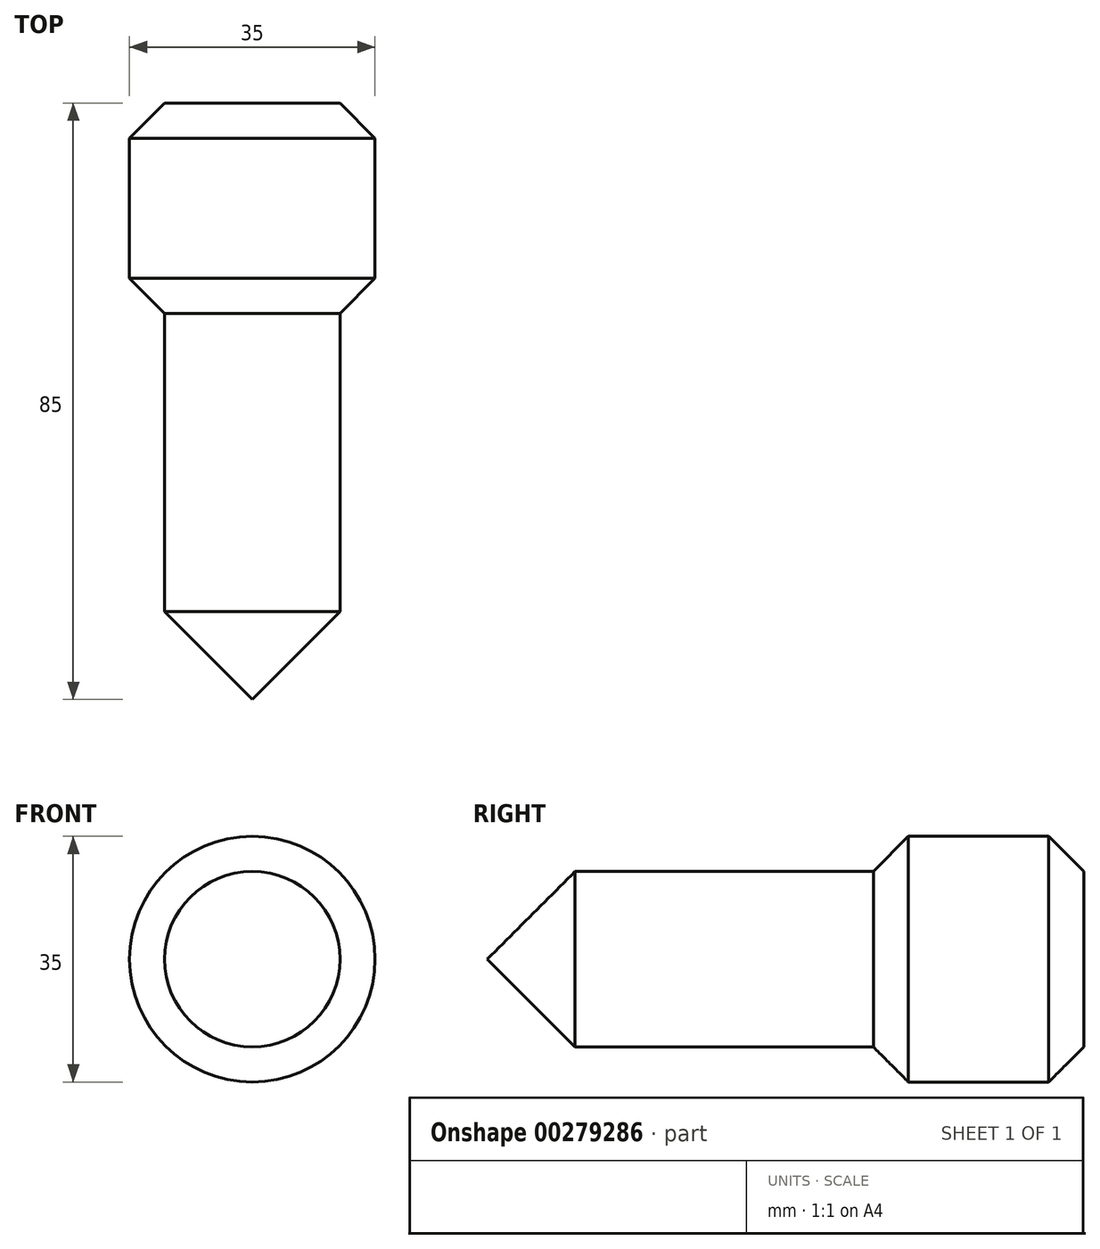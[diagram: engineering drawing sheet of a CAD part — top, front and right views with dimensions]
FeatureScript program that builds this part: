
annotation { "Feature Type Name" : "Feature", "Feature Type Description" : "" }
export const myFeature = defineFeature(function(context is Context, id is Id, definition is map)
    precondition{}
    {
        {
            var Q0;
            Q0=qCreatedBy(makeId("Front.planeOp"),FACE);
            var sketch = newSketch(context, id + "F0", { "sketchPlane" : qUnion([Q0])});
            skCircle(sketch, "E0", {"center": v(0, 0) * mm, "radius": 17.5 * mm});
            skSolve(sketch);
        }
        {
            var Q0;
            Q0 = qSketchRegion(id + "F0", true);
            extrude(context, id + "F1", {"entities" : qUnion([Q0]), "depth" : 30 * mm});
        }
        {
            var Q0;
            Q0=makeQuery(id+"F1.opExtrude","SWEPT_FACE",FACE,{"disambiguationData":[OSD([sQuery(id+"F0.wireOp",EDGE,"E0")])]});
            chamfer(context, id + "F2", {"entities" : qUnion([Q0]), "width" : 5 * mm, "tangentPropagation" : true});
        }
        {
            var Q0;
            Q0=qCreatedBy(makeId("Front.planeOp"),FACE);
            var sketch = newSketch(context, id + "F3", { "sketchPlane" : qUnion([Q0])});
            skCircle(sketch, "E1", {"center": v(0, 0) * mm, "radius": 8.75 * mm});
            skSolve(sketch);
        }
        {
            var Q0;
            Q0 = qSketchRegion(id + "F3", true);
            var Q1;
            Q1=makeQuery(id+"F1.opExtrude","CAP_FACE",FACE,{"disambiguationData":[OSD([sQuery(id+"F0.wireOp",EDGE,"E0")])],"isStart":false});
            extrude(context, id + "F4", {"entities" : qUnion([Q0, Q1]), "operationType" : NewBodyOperationType.ADD, "depth" : 55 * mm});
        }
        {
            var Q0;
            Q0=makeQuery(id+"F4.opExtrude","CAP_FACE",FACE,{"disambiguationData":[OSD([sQuery(id+"F0.wireOp",EDGE,"E0")])],"isStart":false});
            chamfer(context, id + "F5", {"entities" : qUnion([Q0]), "width" : 12.5 * mm, "tangentPropagation" : true});
        }
    });
